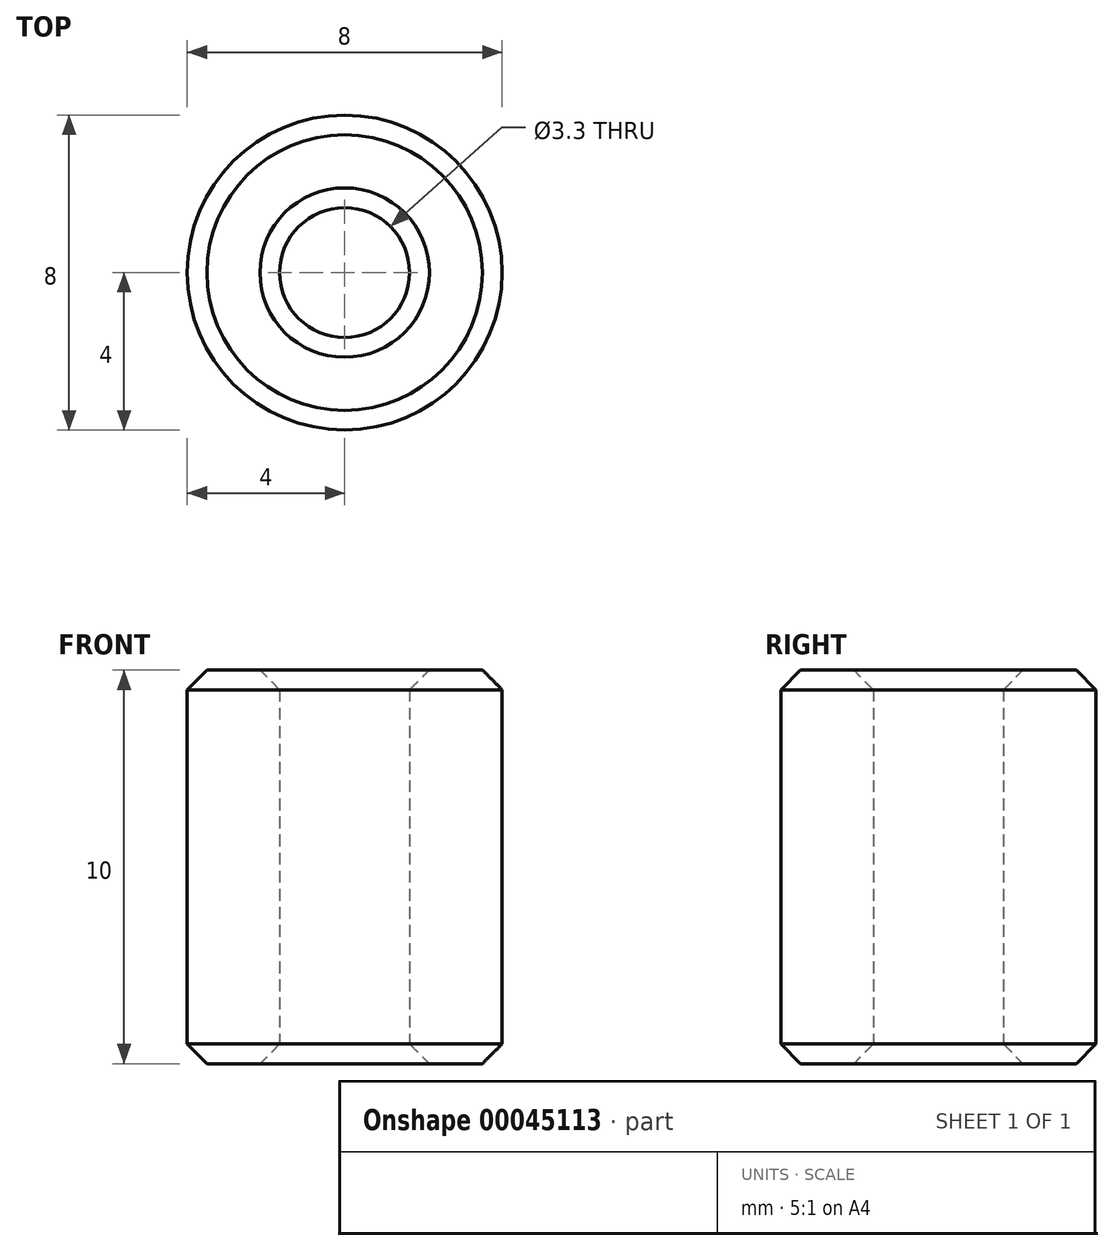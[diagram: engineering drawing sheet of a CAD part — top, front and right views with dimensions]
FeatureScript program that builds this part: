
annotation { "Feature Type Name" : "Feature", "Feature Type Description" : "" }
export const myFeature = defineFeature(function(context is Context, id is Id, definition is map)
    precondition{}
    {
        {
            var Q0;
            Q0=qCreatedBy(makeId("Top.planeOp"),FACE);
            var sketch = newSketch(context, id + "F0", { "sketchPlane" : qUnion([Q0])});
            skCircle(sketch, "E0", {"center": v(0, 0) * mm, "radius": 4 * mm});
            skCircle(sketch, "E1", {"center": v(0, 0) * mm, "radius": 1.65 * mm});
            skSolve(sketch);
        }
        {
            var Q0;
            Q0=makeQuery(id+"F0.imprint","IMPRINT",FACE,{"disambiguationData":[TD([[makeQuery(id+"F0.imprint","IMPRINT",EDGE,{"derivedFrom":sQuery(id+"F0.wireOp",EDGE,"E0")}),1.0]])]});
            extrude(context, id + "F1", {"entities" : qUnion([Q0]), "depth" : 10 * mm});
        }
        {
            var Q0;
            Q0=makeQuery(id+"F1.opExtrude","CAP_EDGE",EDGE,{"disambiguationData":[OSD([sQuery(id+"F0.wireOp",EDGE,"E0")])],"isStart":false});
            var Q1;
            Q1=makeQuery(id+"F1.opExtrude","CAP_EDGE",EDGE,{"disambiguationData":[OSD([sQuery(id+"F0.wireOp",EDGE,"E1")])],"isStart":false});
            var Q2;
            Q2=makeQuery(id+"F1.opExtrude","CAP_EDGE",EDGE,{"disambiguationData":[OSD([sQuery(id+"F0.wireOp",EDGE,"E0")])],"isStart":true});
            var Q3;
            Q3=makeQuery(id+"F1.opExtrude","CAP_EDGE",EDGE,{"disambiguationData":[OSD([sQuery(id+"F0.wireOp",EDGE,"E1")])],"isStart":true});
            chamfer(context, id + "F2", {"entities" : qUnion([Q0, Q1, Q2, Q3]), "width" : .5 * mm, "tangentPropagation" : true});
        }
    });
